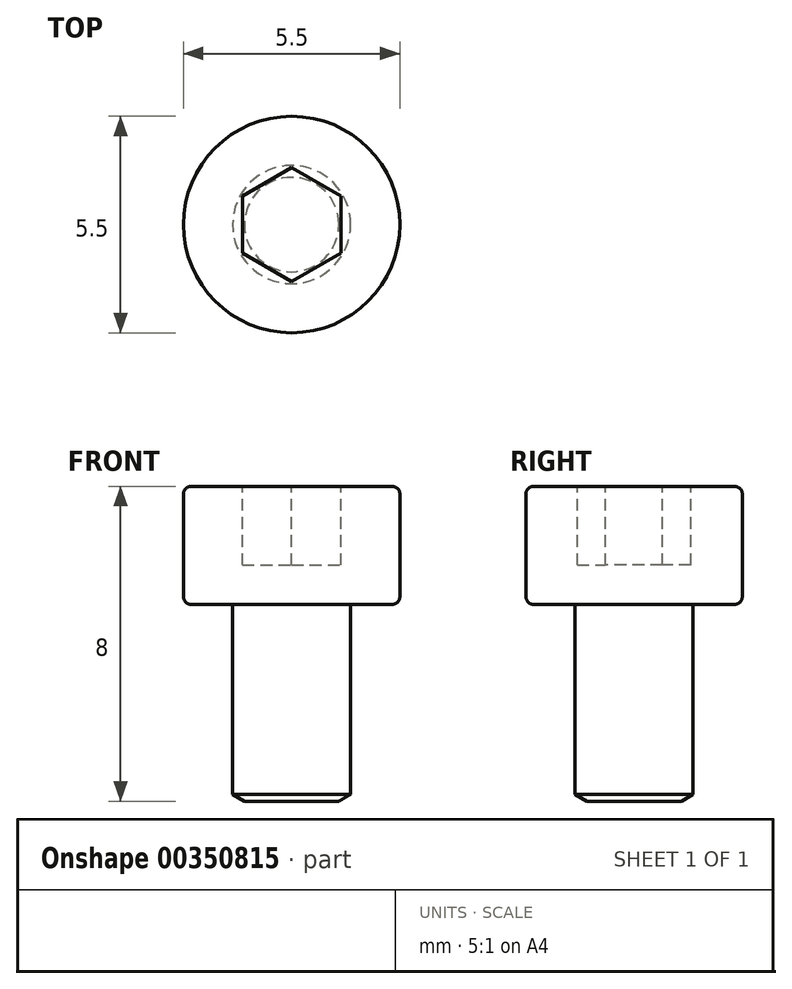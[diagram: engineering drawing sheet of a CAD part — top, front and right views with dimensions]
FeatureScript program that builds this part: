
annotation { "Feature Type Name" : "Feature", "Feature Type Description" : "" }
export const myFeature = defineFeature(function(context is Context, id is Id, definition is map)
    precondition{}
    {
        {
            var Q0;
            Q0=qCreatedBy(makeId("Front.planeOp"),FACE);
            var sketch = newSketch(context, id + "F0", { "sketchPlane" : qUnion([Q0])});
            skLineSegment(sketch, "E0", {"start": v(0, 3.32) * mm, "end": v(0, -24.56) * mm, "construction": true});
            skLineSegment(sketch, "E1", {"start": v(0, 0) * mm, "end": v(2.55, 0) * mm});
            skLineSegment(sketch, "E2", {"start": v(2.75, -0.2) * mm, "end": v(2.75, -2.8) * mm});
            skLineSegment(sketch, "E3", {"start": v(2.55, -3) * mm, "end": v(1.5, -3) * mm});
            skLineSegment(sketch, "E4", {"start": v(1.5, -3) * mm, "end": v(1.5, -7.83) * mm});
            skLineSegment(sketch, "E5", {"start": v(1.2, -8) * mm, "end": v(0, -8) * mm});
            skLineSegment(sketch, "E6", {"start": v(0, -8) * mm, "end": v(0, 0) * mm});
            skPoint(sketch, "E7.visualSharp", {"position": v(2.75, 0) * mm});
            skArc(sketch, "E7.filletArc", {"start": v(2.75, -0.2) * mm, "mid": v(2.7, -0.06) * mm, "end": v(2.55, 0) * mm});
            skPoint(sketch, "E8.visualSharp", {"position": v(2.75, -3) * mm});
            skArc(sketch, "E8.filletArc", {"start": v(2.55, -3) * mm, "mid": v(2.7, -2.94) * mm, "end": v(2.75, -2.8) * mm});
            skLineSegment(sketch, "E9", {"start": v(1.2, -8) * mm, "end": v(1.5, -7.83) * mm});
            skSolve(sketch);
        }
        {
            var Q0;
            Q0 = qSketchRegion(id + "F0", true);
            var Q1;
            Q1=sQuery(id+"F0.wireOp",EDGE,"E0");
            revolve(context, id + "F1", {"entities" : qUnion([Q0]), "axis" : qUnion([Q1]), "revolveType" : RevolveType.FULL});
        }
        {
            var Q0;
            Q0=makeQuery(id+"F1.opRevolve","SWEPT_FACE",FACE,{"disambiguationData":[OSD([sQuery(id+"F0.wireOp",EDGE,"E1")])]});
            var sketch = newSketch(context, id + "F2", { "sketchPlane" : qUnion([Q0])});
            skCircle(sketch, "E10.cCircle", {"center": v(0, 0) * mm, "radius": 1.25 * mm, "construction": true});
            skLineSegment(sketch, "E10.0", {"start": v(1.25, 0.72) * mm, "end": v(1.25, -0.72) * mm});
            skLineSegment(sketch, "E10.1", {"start": v(1.25, -0.72) * mm, "end": v(0, -1.44) * mm});
            skLineSegment(sketch, "E10.2", {"start": v(0, -1.44) * mm, "end": v(-1.25, -0.72) * mm});
            skLineSegment(sketch, "E10.3", {"start": v(-1.25, -0.72) * mm, "end": v(-1.25, 0.72) * mm});
            skLineSegment(sketch, "E10.4", {"start": v(-1.25, 0.72) * mm, "end": v(0, 1.44) * mm});
            skLineSegment(sketch, "E10.5", {"start": v(0, 1.44) * mm, "end": v(1.25, 0.72) * mm});
            skPoint(sketch, "E10.0.midPoint", {"position": v(1.25, 0) * mm});
            skSolve(sketch);
        }
        {
            var Q0;
            Q0 = qSketchRegion(id + "F2", true);
            extrude(context, id + "F3", {"entities" : qUnion([Q0]), "operationType" : NewBodyOperationType.REMOVE, "oppositeDirection" : true, "depth" : 2 * mm});
        }
    });
